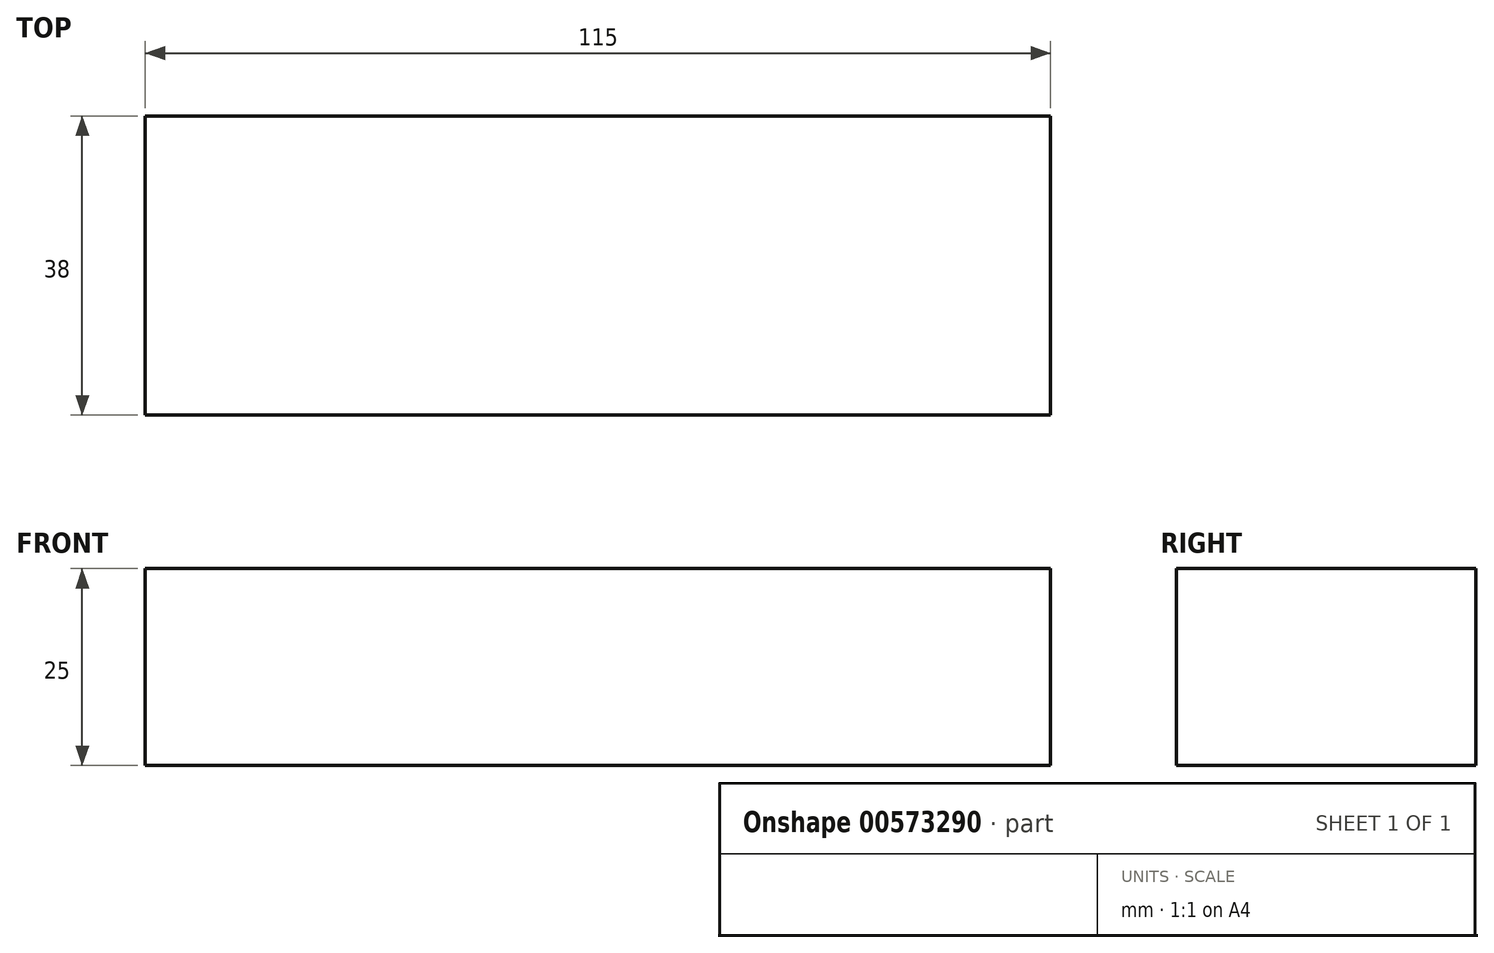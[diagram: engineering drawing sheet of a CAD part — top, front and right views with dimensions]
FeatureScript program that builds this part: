
annotation { "Feature Type Name" : "Feature", "Feature Type Description" : "" }
export const myFeature = defineFeature(function(context is Context, id is Id, definition is map)
    precondition{}
    {
        {
            var Q0;
            Q0=qCreatedBy(makeId("Top.planeOp"),FACE);
            var sketch = newSketch(context, id + "F0", { "sketchPlane" : qUnion([Q0])});
            skLineSegment(sketch, "E0.bottom", {"start": v(-51.33, -28.28) * mm, "end": v(63.67, -28.28) * mm});
            skLineSegment(sketch, "E0.top", {"start": v(-51.33, 9.72) * mm, "end": v(63.67, 9.72) * mm});
            skLineSegment(sketch, "E0.left", {"start": v(-51.33, -28.28) * mm, "end": v(-51.33, 9.72) * mm});
            skLineSegment(sketch, "E0.right", {"start": v(63.67, -28.28) * mm, "end": v(63.67, 9.72) * mm});
            skSolve(sketch);
        }
        {
            var Q0;
            Q0=makeQuery(id+"F0.imprint","IMPRINT",FACE,{"disambiguationData":[TD([[makeQuery(id+"F0.imprint","IMPRINT",EDGE,{"derivedFrom":sQuery(id+"F0.wireOp",EDGE,"E0.bottom")}),1.0]])]});
            extrude(context, id + "F1", {"entities" : qUnion([Q0]), "depth" : 25 * mm, "offsetDistance" : 25 * mm});
        }
    });
